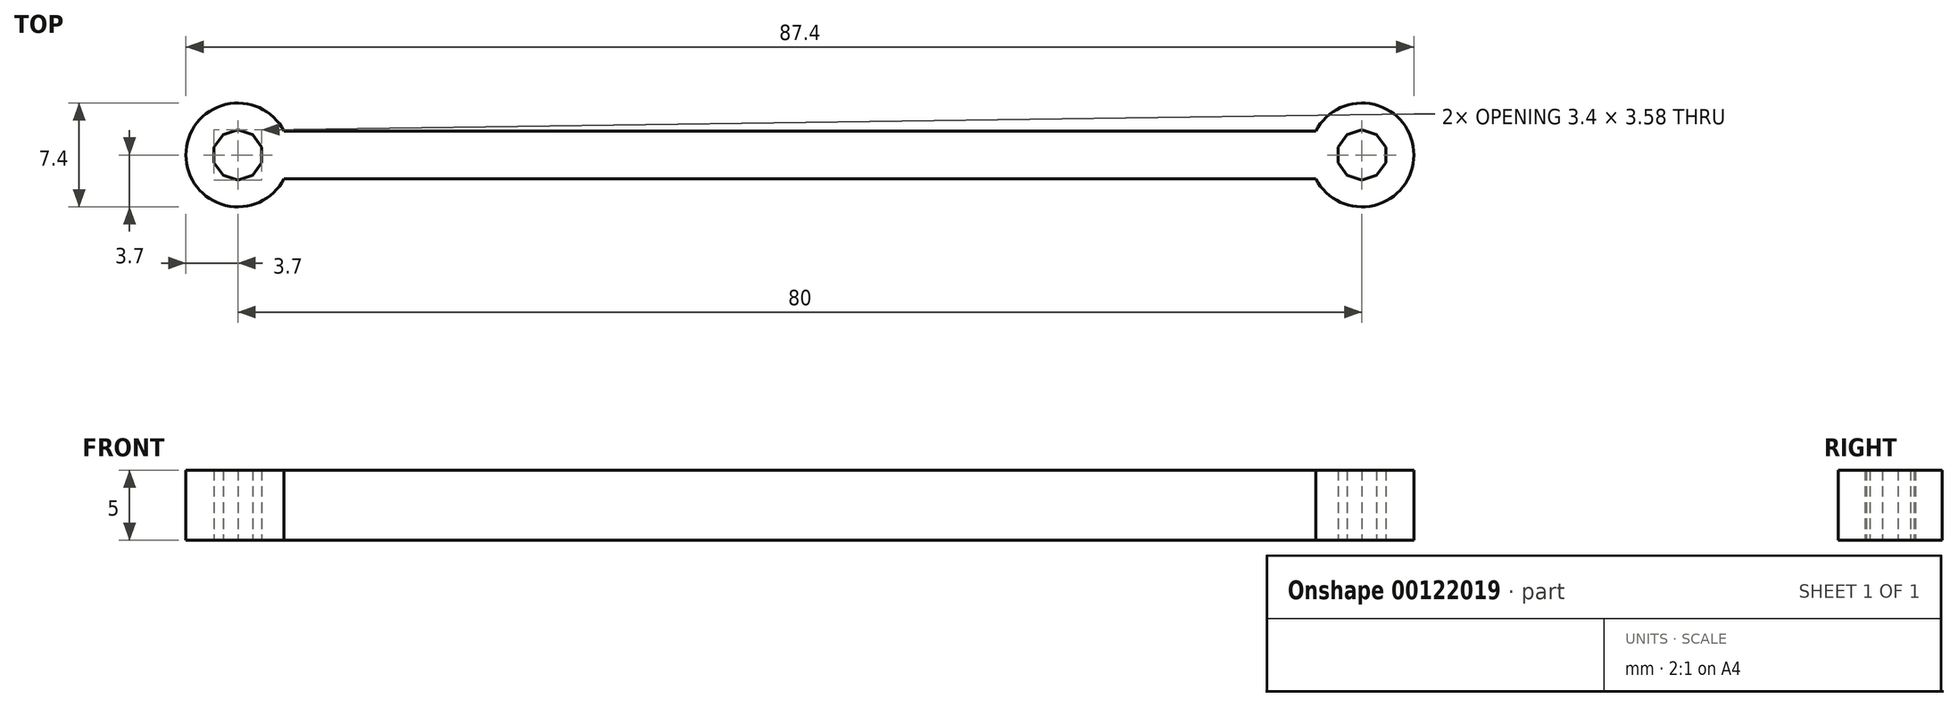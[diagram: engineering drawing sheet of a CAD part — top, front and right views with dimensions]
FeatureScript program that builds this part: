
annotation { "Feature Type Name" : "Feature", "Feature Type Description" : "" }
export const myFeature = defineFeature(function(context is Context, id is Id, definition is map)
    precondition{}
    {
        {
            var Q0;
            Q0=qCreatedBy(makeId("Top.planeOp"),FACE);
            var sketch = newSketch(context, id + "F0", { "sketchPlane" : qUnion([Q0])});
            skCircle(sketch, "E0", {"center": v(-40, 0) * mm, "radius": 1.7 * mm, "construction": true});
            skCircle(sketch, "E1", {"center": v(40, 0) * mm, "radius": 1.7 * mm, "construction": true});
            skArc(sketch, "E2.0", {"start": v(-36.71, 1.7) * mm, "mid": v(-43.7, 0) * mm, "end": v(-36.71, -1.7) * mm});
            skArc(sketch, "E3.0", {"start": v(36.71, -1.7) * mm, "mid": v(43.7, 0) * mm, "end": v(36.71, 1.7) * mm});
            skPoint(sketch, "E4", {"position": v(-40, 1.7) * mm});
            skPoint(sketch, "E5", {"position": v(-40, -1.7) * mm});
            skPoint(sketch, "E6", {"position": v(40, 1.7) * mm});
            skPoint(sketch, "E7", {"position": v(40, -1.7) * mm});
            skLineSegment(sketch, "E8", {"start": v(-36.71, 1.7) * mm, "end": v(36.71, 1.7) * mm});
            skLineSegment(sketch, "E9", {"start": v(36.71, -1.7) * mm, "end": v(-36.71, -1.7) * mm});
            skLineSegment(sketch, "E10.0", {"start": v(-41.7, -0.55) * mm, "end": v(-41.7, 0.55) * mm});
            skLineSegment(sketch, "E10.1", {"start": v(-41.7, 0.55) * mm, "end": v(-41.05, 1.45) * mm});
            skLineSegment(sketch, "E10.2", {"start": v(-41.05, 1.45) * mm, "end": v(-40, 1.79) * mm});
            skLineSegment(sketch, "E10.3", {"start": v(-40, 1.79) * mm, "end": v(-38.95, 1.45) * mm});
            skLineSegment(sketch, "E10.4", {"start": v(-38.95, 1.45) * mm, "end": v(-38.3, 0.55) * mm});
            skLineSegment(sketch, "E10.5", {"start": v(-38.3, 0.55) * mm, "end": v(-38.3, -0.55) * mm});
            skLineSegment(sketch, "E10.6", {"start": v(-38.3, -0.55) * mm, "end": v(-38.95, -1.45) * mm});
            skLineSegment(sketch, "E10.7", {"start": v(-38.95, -1.45) * mm, "end": v(-40, -1.79) * mm});
            skLineSegment(sketch, "E10.8", {"start": v(-40, -1.79) * mm, "end": v(-41.05, -1.45) * mm});
            skLineSegment(sketch, "E10.9", {"start": v(-41.05, -1.45) * mm, "end": v(-41.7, -0.55) * mm});
            skPoint(sketch, "E10.0.midPoint", {"position": v(-41.7, 0) * mm});
            skLineSegment(sketch, "E11.0", {"start": v(41.7, 0.55) * mm, "end": v(41.7, -0.55) * mm});
            skLineSegment(sketch, "E11.1", {"start": v(41.7, -0.55) * mm, "end": v(41.05, -1.45) * mm});
            skLineSegment(sketch, "E11.2", {"start": v(41.05, -1.45) * mm, "end": v(40, -1.79) * mm});
            skLineSegment(sketch, "E11.3", {"start": v(40, -1.79) * mm, "end": v(38.95, -1.45) * mm});
            skLineSegment(sketch, "E11.4", {"start": v(38.95, -1.45) * mm, "end": v(38.3, -0.55) * mm});
            skLineSegment(sketch, "E11.5", {"start": v(38.3, -0.55) * mm, "end": v(38.3, 0.55) * mm});
            skLineSegment(sketch, "E11.6", {"start": v(38.3, 0.55) * mm, "end": v(38.95, 1.45) * mm});
            skLineSegment(sketch, "E11.7", {"start": v(38.95, 1.45) * mm, "end": v(40, 1.79) * mm});
            skLineSegment(sketch, "E11.8", {"start": v(40, 1.79) * mm, "end": v(41.05, 1.45) * mm});
            skLineSegment(sketch, "E11.9", {"start": v(41.05, 1.45) * mm, "end": v(41.7, 0.55) * mm});
            skPoint(sketch, "E11.0.midPoint", {"position": v(41.7, 0) * mm});
            skSolve(sketch);
        }
        {
            var Q0;
            Q0=makeQuery(id+"F0.imprint","IMPRINT",FACE,{"disambiguationData":[TD([[makeQuery(id+"F0.imprint","IMPRINT",EDGE,{"derivedFrom":sQuery(id+"F0.wireOp",EDGE,"E2.0")}),1.0]])]});
            extrude(context, id + "F1", {"entities" : qUnion([Q0]), "depth" : 5 * mm});
        }
    });
